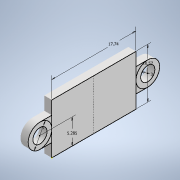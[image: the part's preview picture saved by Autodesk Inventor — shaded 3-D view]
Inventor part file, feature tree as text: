
AUTODESK INVENTOR PART (.ipt)
format: ipt  version: 2022 (Build 260153070, 153G)  size: 125,440 bytes
history: native  units: in
note: dims shown in document units (in); Inventor stores cm internally (conversion verified against a paired STEP export)
features: sketch x1, extrude x1
ambient origin geometry x8: Origin, YZ Plane, XZ Plane, XY Plane, X Axis, Y Axis, Z Axis, Center Point
bodies: Solid1 (feature_tree)
feature tree (2):
  sketch  "Sketch1"  dims[d0=0.6984in d1=0.4161in d2=0.2081in d3=0.1969in d7=0.0618in d8=0.0in d11=0.1181in]
  extrude  "Extrusion1"  Depth=0.4161in
